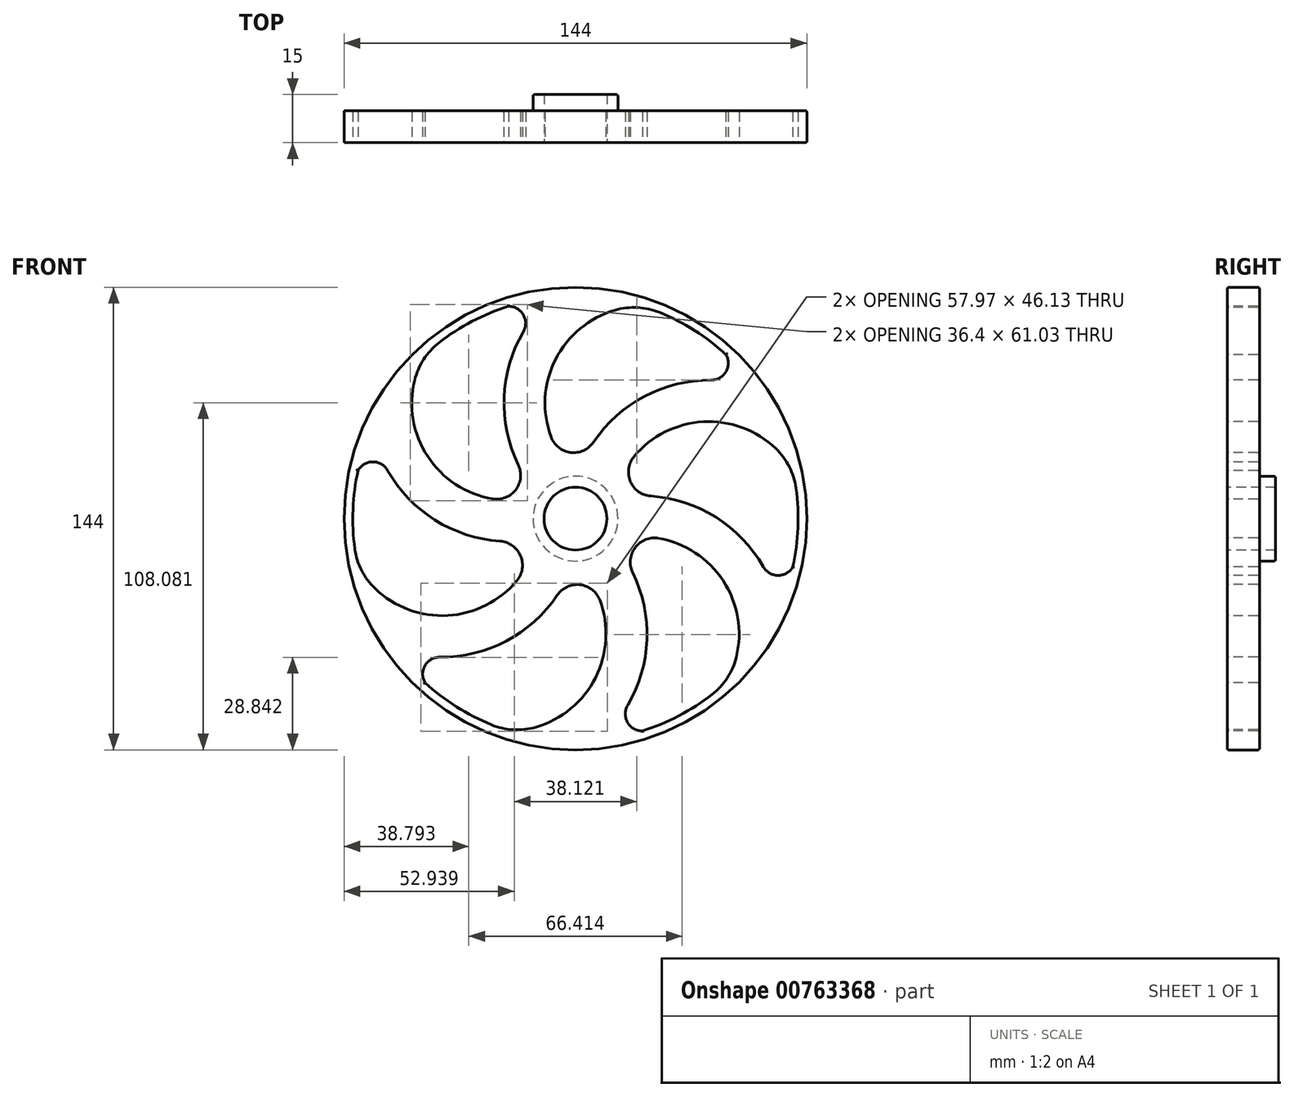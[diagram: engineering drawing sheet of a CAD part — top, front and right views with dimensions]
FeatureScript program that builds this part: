
annotation { "Feature Type Name" : "Feature", "Feature Type Description" : "" }
export const myFeature = defineFeature(function(context is Context, id is Id, definition is map)
    precondition{}
    {
        {
            var Q0;
            Q0=qCreatedBy(makeId("Front.planeOp"),FACE);
            var sketch = newSketch(context, id + "F0", { "sketchPlane" : qUnion([Q0])});
            skCircle(sketch, "E0", {"center": v(0, 0) * mm, "radius": 75 * mm});
            skCircle(sketch, "E1", {"center": v(0, 0) * mm, "radius": 72 * mm});
            skCircle(sketch, "E2", {"center": v(0, 0) * mm, "radius": 9.8 * mm});
            skCircle(sketch, "E3", {"center": v(0, 0) * mm, "radius": 13.2 * mm});
            skLineSegment(sketch, "E4", {"start": v(0, 0) * mm, "end": v(0, 101.76) * mm, "construction": true});
            skLineSegment(sketch, "E5", {"start": v(0, 0) * mm, "end": v(56.87, 98.5) * mm, "construction": true});
            skLineSegment(sketch, "E6", {"start": v(0, 0) * mm, "end": v(-56.77, 98.34) * mm, "construction": true});
            skLineSegment(sketch, "E7", {"start": v(-20.83, 66.1) * mm, "end": v(-20.83, 66.1) * mm});
            skArc(sketch, "E8", {"start": v(-20.83, 66.1) * mm, "mid": v(-32.17, 61.38) * mm, "end": v(-42.5, 54.74) * mm});
            skArc(sketch, "E9.trimOffspring", {"start": v(-16.24, 58.11) * mm, "mid": v(-22.22, 37.66) * mm, "end": v(-17.82, 16.81) * mm});
            skArc(sketch, "E10.trimOffspring", {"start": v(-50.05, 43.11) * mm, "mid": v(-45.99, 19.35) * mm, "end": v(-25.83, 6.13) * mm});
            skPoint(sketch, "E11.visualSharp", {"position": v(-11.53, 64.66) * mm});
            skArc(sketch, "E11.filletArc", {"start": v(-16.24, 58.11) * mm, "mid": v(-16.21, 63.44) * mm, "end": v(-20.83, 66.1) * mm});
            skPoint(sketch, "E12.visualSharp", {"position": v(-11.4, 7.17) * mm});
            skArc(sketch, "E12.filletArc", {"start": v(-25.83, 6.13) * mm, "mid": v(-18.56, 9.03) * mm, "end": v(-17.82, 16.81) * mm});
            skPoint(sketch, "E13.visualSharp", {"position": v(-46.83, 51.08) * mm});
            skArc(sketch, "E13.filletArc", {"start": v(-42.5, 54.74) * mm, "mid": v(-47.26, 49.56) * mm, "end": v(-50.05, 43.11) * mm});
            skArc(sketch, "E14.1.0", {"start": v(-67.65, 15.01) * mm, "mid": v(-69.24, 2.83) * mm, "end": v(-68.65, -9.44) * mm});
            skArc(sketch, "E14.1.1", {"start": v(-68.65, -9.44) * mm, "mid": v(-66.55, -16.15) * mm, "end": v(-62.36, -21.8) * mm});
            skArc(sketch, "E14.1.2", {"start": v(-62.36, -21.8) * mm, "mid": v(-39.75, -30.15) * mm, "end": v(-18.23, -19.3) * mm});
            skArc(sketch, "E14.1.3", {"start": v(-18.23, -19.3) * mm, "mid": v(-17.1, -11.56) * mm, "end": v(-23.47, -7.03) * mm});
            skArc(sketch, "E14.1.4", {"start": v(-58.45, 15) * mm, "mid": v(-43.73, -0.41) * mm, "end": v(-23.47, -7.03) * mm});
            skArc(sketch, "E14.1.5", {"start": v(-58.45, 15) * mm, "mid": v(-63.05, 17.68) * mm, "end": v(-67.65, 15.01) * mm});
            skArc(sketch, "E14.2.0", {"start": v(-46.83, -51.08) * mm, "mid": v(-37.07, -58.55) * mm, "end": v(-26.15, -64.18) * mm});
            skArc(sketch, "E14.2.1", {"start": v(-26.15, -64.18) * mm, "mid": v(-19.3, -65.7) * mm, "end": v(-12.3, -64.9) * mm});
            skArc(sketch, "E14.2.2", {"start": v(-12.3, -64.9) * mm, "mid": v(6.24, -49.5) * mm, "end": v(7.6, -25.44) * mm});
            skArc(sketch, "E14.2.3", {"start": v(7.6, -25.44) * mm, "mid": v(1.46, -20.59) * mm, "end": v(-5.65, -23.84) * mm});
            skArc(sketch, "E14.2.4", {"start": v(-42.2, -43.12) * mm, "mid": v(-21.5, -38.08) * mm, "end": v(-5.65, -23.84) * mm});
            skArc(sketch, "E14.2.5", {"start": v(-42.2, -43.12) * mm, "mid": v(-46.83, -45.76) * mm, "end": v(-46.83, -51.08) * mm});
            skArc(sketch, "E14.3.0", {"start": v(20.83, -66.1) * mm, "mid": v(32.17, -61.38) * mm, "end": v(42.5, -54.74) * mm});
            skArc(sketch, "E14.3.1", {"start": v(42.5, -54.74) * mm, "mid": v(47.26, -49.56) * mm, "end": v(50.05, -43.11) * mm});
            skArc(sketch, "E14.3.2", {"start": v(50.05, -43.11) * mm, "mid": v(45.99, -19.35) * mm, "end": v(25.83, -6.13) * mm});
            skArc(sketch, "E14.3.3", {"start": v(25.83, -6.13) * mm, "mid": v(18.56, -9.03) * mm, "end": v(17.82, -16.81) * mm});
            skArc(sketch, "E14.3.4", {"start": v(16.24, -58.11) * mm, "mid": v(22.22, -37.66) * mm, "end": v(17.82, -16.81) * mm});
            skArc(sketch, "E14.3.5", {"start": v(16.24, -58.11) * mm, "mid": v(16.21, -63.44) * mm, "end": v(20.83, -66.1) * mm});
            skArc(sketch, "E14.4.0", {"start": v(67.65, -15.01) * mm, "mid": v(69.24, -2.83) * mm, "end": v(68.65, 9.44) * mm});
            skArc(sketch, "E14.4.1", {"start": v(68.65, 9.44) * mm, "mid": v(66.55, 16.15) * mm, "end": v(62.36, 21.8) * mm});
            skArc(sketch, "E14.4.2", {"start": v(62.36, 21.8) * mm, "mid": v(39.75, 30.15) * mm, "end": v(18.23, 19.3) * mm});
            skArc(sketch, "E14.4.3", {"start": v(18.23, 19.3) * mm, "mid": v(17.1, 11.56) * mm, "end": v(23.47, 7.03) * mm});
            skArc(sketch, "E14.4.4", {"start": v(58.45, -15) * mm, "mid": v(43.73, 0.41) * mm, "end": v(23.47, 7.03) * mm});
            skArc(sketch, "E14.4.5", {"start": v(58.45, -15) * mm, "mid": v(63.05, -17.68) * mm, "end": v(67.65, -15.01) * mm});
            skArc(sketch, "E14.5.0", {"start": v(46.83, 51.08) * mm, "mid": v(37.07, 58.55) * mm, "end": v(26.15, 64.18) * mm});
            skArc(sketch, "E14.5.1", {"start": v(26.15, 64.18) * mm, "mid": v(19.3, 65.7) * mm, "end": v(12.3, 64.9) * mm});
            skArc(sketch, "E14.5.2", {"start": v(12.3, 64.9) * mm, "mid": v(-6.24, 49.5) * mm, "end": v(-7.6, 25.44) * mm});
            skArc(sketch, "E14.5.3", {"start": v(-7.6, 25.44) * mm, "mid": v(-1.46, 20.59) * mm, "end": v(5.65, 23.84) * mm});
            skArc(sketch, "E14.5.4", {"start": v(42.2, 43.12) * mm, "mid": v(21.5, 38.08) * mm, "end": v(5.65, 23.84) * mm});
            skArc(sketch, "E14.5.5", {"start": v(42.2, 43.12) * mm, "mid": v(46.83, 45.76) * mm, "end": v(46.83, 51.08) * mm});
            skSolve(sketch);
        }
        {
            var Q0;
            Q0=makeQuery(id+"F0.imprint","IMPRINT",FACE,{"disambiguationData":[TD([[makeQuery(id+"F0.imprint","IMPRINT",EDGE,{"derivedFrom":sQuery(id+"F0.wireOp",EDGE,"E1")}),1.0]])]});
            extrude(context, id + "F1", {"entities" : qUnion([Q0]), "oppositeDirection" : true, "depth" : 10 * mm, "offsetDistance" : 25 * mm});
        }
        {
            var Q0;
            Q0=makeQuery(id+"F1.opExtrude","CAP_FACE",FACE,{"disambiguationData":[OSD([sQuery(id+"F0.wireOp",EDGE,"E1"),sQuery(id+"F0.wireOp",EDGE,"E3"),sQuery(id+"F0.wireOp",EDGE,"E8"),sQuery(id+"F0.wireOp",EDGE,"E9.trimOffspring"),sQuery(id+"F0.wireOp",EDGE,"E10.trimOffspring"),sQuery(id+"F0.wireOp",EDGE,"E11.filletArc"),sQuery(id+"F0.wireOp",EDGE,"E12.filletArc"),sQuery(id+"F0.wireOp",EDGE,"E13.filletArc"),sQuery(id+"F0.wireOp",EDGE,"E14.1.0"),sQuery(id+"F0.wireOp",EDGE,"E14.1.1"),sQuery(id+"F0.wireOp",EDGE,"E14.1.2"),sQuery(id+"F0.wireOp",EDGE,"E14.1.3"),sQuery(id+"F0.wireOp",EDGE,"E14.1.4"),sQuery(id+"F0.wireOp",EDGE,"E14.1.5"),sQuery(id+"F0.wireOp",EDGE,"E14.2.0"),sQuery(id+"F0.wireOp",EDGE,"E14.2.1"),sQuery(id+"F0.wireOp",EDGE,"E14.2.2"),sQuery(id+"F0.wireOp",EDGE,"E14.2.3"),sQuery(id+"F0.wireOp",EDGE,"E14.2.4"),sQuery(id+"F0.wireOp",EDGE,"E14.2.5"),sQuery(id+"F0.wireOp",EDGE,"E14.3.0"),sQuery(id+"F0.wireOp",EDGE,"E14.3.1"),sQuery(id+"F0.wireOp",EDGE,"E14.3.2"),sQuery(id+"F0.wireOp",EDGE,"E14.3.3"),sQuery(id+"F0.wireOp",EDGE,"E14.3.4"),sQuery(id+"F0.wireOp",EDGE,"E14.3.5"),sQuery(id+"F0.wireOp",EDGE,"E14.4.0"),sQuery(id+"F0.wireOp",EDGE,"E14.4.1"),sQuery(id+"F0.wireOp",EDGE,"E14.4.2"),sQuery(id+"F0.wireOp",EDGE,"E14.4.3"),sQuery(id+"F0.wireOp",EDGE,"E14.4.4"),sQuery(id+"F0.wireOp",EDGE,"E14.4.5"),sQuery(id+"F0.wireOp",EDGE,"E14.5.0"),sQuery(id+"F0.wireOp",EDGE,"E14.5.1"),sQuery(id+"F0.wireOp",EDGE,"E14.5.2"),sQuery(id+"F0.wireOp",EDGE,"E14.5.3"),sQuery(id+"F0.wireOp",EDGE,"E14.5.4"),sQuery(id+"F0.wireOp",EDGE,"E14.5.5")])],"isStart":true});
            var sketch = newSketch(context, id + "F2", { "sketchPlane" : qUnion([Q0])});
            skCircle(sketch, "E15", {"center": v(0, 0) * mm, "radius": 9.8 * mm});
            skSolve(sketch);
        }
        {
            var Q0;
            Q0=makeQuery(id+"F2.imprint","IMPRINT",FACE,{"disambiguationData":[TD([[makeQuery(id+"F2.imprint","IMPRINT",EDGE,{"derivedFrom":sQuery(id+"F2.wireOp",EDGE,"E15")}),-1.0]])]});
            extrude(context, id + "F3", {"entities" : qUnion([Q0]), "operationType" : NewBodyOperationType.ADD, "oppositeDirection" : true, "depth" : 15 * mm, "offsetDistance" : 25 * mm});
        }
        {
            var Q0;
            Q0=makeQuery(id+"F3.opExtrude","SWEPT_FACE",FACE,{"disambiguationData":[OSD([sQuery(id+"F0.wireOp",EDGE,"E3")])]});
            var Q1;
            Q1=makeQuery(id+"F1.opExtrude","CAP_FACE",FACE,{"disambiguationData":[OSD([sQuery(id+"F0.wireOp",EDGE,"E1"),sQuery(id+"F0.wireOp",EDGE,"E3"),sQuery(id+"F0.wireOp",EDGE,"E8"),sQuery(id+"F0.wireOp",EDGE,"E9.trimOffspring"),sQuery(id+"F0.wireOp",EDGE,"E10.trimOffspring"),sQuery(id+"F0.wireOp",EDGE,"E11.filletArc"),sQuery(id+"F0.wireOp",EDGE,"E12.filletArc"),sQuery(id+"F0.wireOp",EDGE,"E13.filletArc"),sQuery(id+"F0.wireOp",EDGE,"E14.1.0"),sQuery(id+"F0.wireOp",EDGE,"E14.1.1"),sQuery(id+"F0.wireOp",EDGE,"E14.1.2"),sQuery(id+"F0.wireOp",EDGE,"E14.1.3"),sQuery(id+"F0.wireOp",EDGE,"E14.1.4"),sQuery(id+"F0.wireOp",EDGE,"E14.1.5"),sQuery(id+"F0.wireOp",EDGE,"E14.2.0"),sQuery(id+"F0.wireOp",EDGE,"E14.2.1"),sQuery(id+"F0.wireOp",EDGE,"E14.2.2"),sQuery(id+"F0.wireOp",EDGE,"E14.2.3"),sQuery(id+"F0.wireOp",EDGE,"E14.2.4"),sQuery(id+"F0.wireOp",EDGE,"E14.2.5"),sQuery(id+"F0.wireOp",EDGE,"E14.3.0"),sQuery(id+"F0.wireOp",EDGE,"E14.3.1"),sQuery(id+"F0.wireOp",EDGE,"E14.3.2"),sQuery(id+"F0.wireOp",EDGE,"E14.3.3"),sQuery(id+"F0.wireOp",EDGE,"E14.3.4"),sQuery(id+"F0.wireOp",EDGE,"E14.3.5"),sQuery(id+"F0.wireOp",EDGE,"E14.4.0"),sQuery(id+"F0.wireOp",EDGE,"E14.4.1"),sQuery(id+"F0.wireOp",EDGE,"E14.4.2"),sQuery(id+"F0.wireOp",EDGE,"E14.4.3"),sQuery(id+"F0.wireOp",EDGE,"E14.4.4"),sQuery(id+"F0.wireOp",EDGE,"E14.4.5"),sQuery(id+"F0.wireOp",EDGE,"E14.5.0"),sQuery(id+"F0.wireOp",EDGE,"E14.5.1"),sQuery(id+"F0.wireOp",EDGE,"E14.5.2"),sQuery(id+"F0.wireOp",EDGE,"E14.5.3"),sQuery(id+"F0.wireOp",EDGE,"E14.5.4"),sQuery(id+"F0.wireOp",EDGE,"E14.5.5")])],"isStart":false});
            fillet(context, id + "F4", {"entities" : qUnion([Q0, Q1]), "radius" : 0.5 * mm, "tangentPropagation" : true, "allowEdgeOverflow" : false});
        }
        {
            var Q0;
            {var subQ0=sQuery(id+"F0.wireOp",EDGE,"E3");Q0=makeQuery(id+"F3.boolean.opBoolean","MERGE",FACE,{"derivedFrom":[makeQuery(id+"F1.opExtrude","CAP_FACE",FACE,{"disambiguationData":[OSD([sQuery(id+"F0.wireOp",EDGE,"E1"),subQ0,sQuery(id+"F0.wireOp",EDGE,"E8"),sQuery(id+"F0.wireOp",EDGE,"E9.trimOffspring"),sQuery(id+"F0.wireOp",EDGE,"E10.trimOffspring"),sQuery(id+"F0.wireOp",EDGE,"E11.filletArc"),sQuery(id+"F0.wireOp",EDGE,"E12.filletArc"),sQuery(id+"F0.wireOp",EDGE,"E13.filletArc"),sQuery(id+"F0.wireOp",EDGE,"E14.1.0"),sQuery(id+"F0.wireOp",EDGE,"E14.1.1"),sQuery(id+"F0.wireOp",EDGE,"E14.1.2"),sQuery(id+"F0.wireOp",EDGE,"E14.1.3"),sQuery(id+"F0.wireOp",EDGE,"E14.1.4"),sQuery(id+"F0.wireOp",EDGE,"E14.1.5"),sQuery(id+"F0.wireOp",EDGE,"E14.2.0"),sQuery(id+"F0.wireOp",EDGE,"E14.2.1"),sQuery(id+"F0.wireOp",EDGE,"E14.2.2"),sQuery(id+"F0.wireOp",EDGE,"E14.2.3"),sQuery(id+"F0.wireOp",EDGE,"E14.2.4"),sQuery(id+"F0.wireOp",EDGE,"E14.2.5"),sQuery(id+"F0.wireOp",EDGE,"E14.3.0"),sQuery(id+"F0.wireOp",EDGE,"E14.3.1"),sQuery(id+"F0.wireOp",EDGE,"E14.3.2"),sQuery(id+"F0.wireOp",EDGE,"E14.3.3"),sQuery(id+"F0.wireOp",EDGE,"E14.3.4"),sQuery(id+"F0.wireOp",EDGE,"E14.3.5"),sQuery(id+"F0.wireOp",EDGE,"E14.4.0"),sQuery(id+"F0.wireOp",EDGE,"E14.4.1"),sQuery(id+"F0.wireOp",EDGE,"E14.4.2"),sQuery(id+"F0.wireOp",EDGE,"E14.4.3"),sQuery(id+"F0.wireOp",EDGE,"E14.4.4"),sQuery(id+"F0.wireOp",EDGE,"E14.4.5"),sQuery(id+"F0.wireOp",EDGE,"E14.5.0"),sQuery(id+"F0.wireOp",EDGE,"E14.5.1"),sQuery(id+"F0.wireOp",EDGE,"E14.5.2"),sQuery(id+"F0.wireOp",EDGE,"E14.5.3"),sQuery(id+"F0.wireOp",EDGE,"E14.5.4"),sQuery(id+"F0.wireOp",EDGE,"E14.5.5")])],"isStart":true}),makeQuery(id+"F3.opExtrude","CAP_FACE",FACE,{"disambiguationData":[OSD([subQ0,sQuery(id+"F2.wireOp",EDGE,"E15")])],"isStart":true})]});}
            fillet(context, id + "F5", {"entities" : qUnion([Q0]), "radius" : 0.5 * mm, "tangentPropagation" : true, "allowEdgeOverflow" : false});
        }
    });
